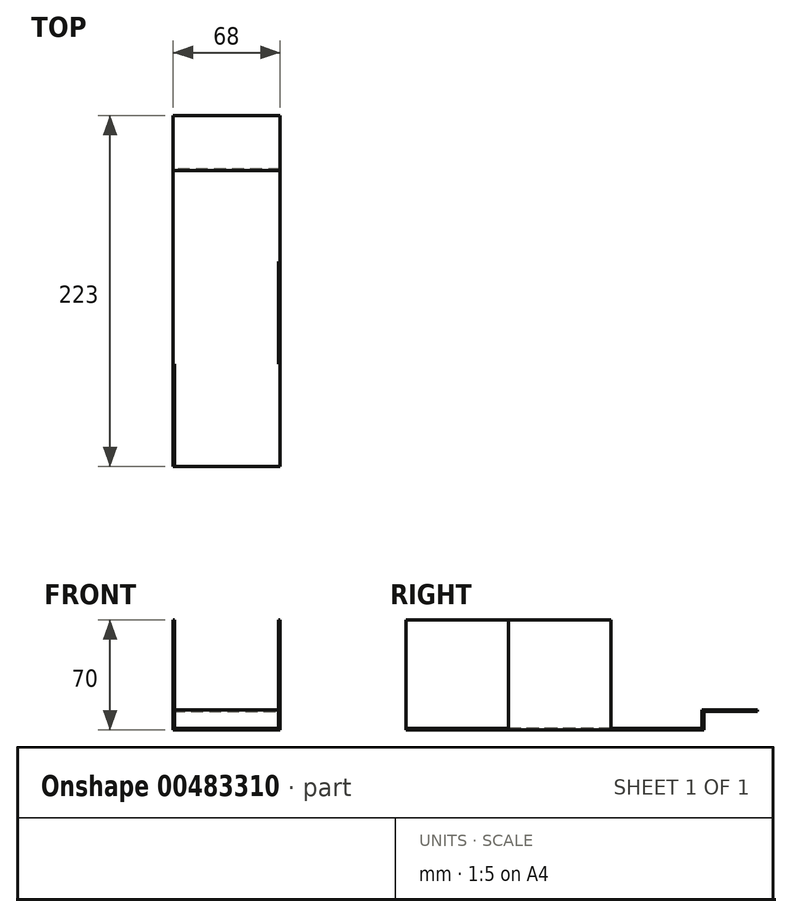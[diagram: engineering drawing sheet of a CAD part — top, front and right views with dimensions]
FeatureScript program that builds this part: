
annotation { "Feature Type Name" : "Feature", "Feature Type Description" : "" }
export const myFeature = defineFeature(function(context is Context, id is Id, definition is map)
    precondition{}
    {
        {
            var Q0;
            Q0=qCreatedBy(makeId("Top.planeOp"),FACE);
            var sketch = newSketch(context, id + "F0", { "sketchPlane" : qUnion([Q0])});
            skLineSegment(sketch, "E0.bottom", {"start": v(111.94, 131.54) * mm, "end": v(179.94, 131.54) * mm});
            skLineSegment(sketch, "E0.top", {"start": v(111.94, -91.46) * mm, "end": v(179.94, -91.46) * mm});
            skLineSegment(sketch, "E0.left", {"start": v(111.94, 131.54) * mm, "end": v(111.94, -91.46) * mm});
            skLineSegment(sketch, "E0.right", {"start": v(179.94, 131.54) * mm, "end": v(179.94, -91.46) * mm});
            skLineSegment(sketch, "E1.top", {"start": v(111.94, 96.54) * mm, "end": v(179.94, 96.54) * mm});
            skLineSegment(sketch, "E1.left", {"start": v(111.94, 131.54) * mm, "end": v(111.94, 96.54) * mm});
            skLineSegment(sketch, "E1.right", {"start": v(179.94, 131.54) * mm, "end": v(179.94, 96.54) * mm});
            skSolve(sketch);
        }
        {
            var Q0;
            Q0=makeQuery(id+"F0.imprint","IMPRINT",FACE,{"disambiguationData":[TD([[makeQuery(id+"F0.imprint","IMPRINT",EDGE,{"derivedFrom":sQuery(id+"F0.wireOp",EDGE,"E0.top")}),1.0]])]});
            extrude(context, id + "F1", {"entities" : qUnion([Q0]), "depth" : 1 * mm});
        }
        {
            var Q0;
            Q0=makeQuery(id+"F0.imprint","IMPRINT",FACE,{"disambiguationData":[TD([[makeQuery(id+"F0.imprint","IMPRINT",EDGE,{"derivedFrom":sQuery(id+"F0.wireOp",EDGE,"E0.bottom")}),-1.0]])]});
            extrude(context, id + "F2", {"entities" : qUnion([Q0]), "operationType" : NewBodyOperationType.ADD, "depth" : 13 * mm});
        }
        {
            var Q0;
            {var subQ0=sQuery(id+"F0.wireOp",EDGE,"E1.top");Q0=makeQuery(id+"F2.boolean.opBoolean","MERGE",FACE,{"derivedFrom":[makeQuery(id+"F1.opExtrude","CAP_FACE",FACE,{"disambiguationData":[OSD([sQuery(id+"F0.wireOp",EDGE,"E0.top"),sQuery(id+"F0.wireOp",EDGE,"E0.left"),sQuery(id+"F0.wireOp",EDGE,"E0.right"),subQ0])],"isStart":true}),makeQuery(id+"F2.opExtrude","CAP_FACE",FACE,{"disambiguationData":[OSD([sQuery(id+"F0.wireOp",EDGE,"E0.bottom"),subQ0,sQuery(id+"F0.wireOp",EDGE,"E1.left"),sQuery(id+"F0.wireOp",EDGE,"E1.right")])],"isStart":true})]});}
            var sketch = newSketch(context, id + "F3", { "sketchPlane" : qUnion([Q0])});
            skLineSegment(sketch, "E2.bottom", {"start": v(179.94, -131.54) * mm, "end": v(111.94, -131.54) * mm});
            skLineSegment(sketch, "E2.top", {"start": v(179.94, -97.54) * mm, "end": v(111.94, -97.54) * mm});
            skLineSegment(sketch, "E2.left", {"start": v(179.94, -131.54) * mm, "end": v(179.94, -97.54) * mm});
            skLineSegment(sketch, "E2.right", {"start": v(111.94, -131.54) * mm, "end": v(111.94, -97.54) * mm});
            skSolve(sketch);
        }
        {
            var Q0;
            Q0=makeQuery(id+"F3.imprint","IMPRINT",FACE,{"disambiguationData":[TD([[makeQuery(id+"F3.imprint","IMPRINT",EDGE,{"derivedFrom":sQuery(id+"F3.wireOp",EDGE,"E2.bottom")}),1.0]])]});
            extrude(context, id + "F4", {"entities" : qUnion([Q0]), "operationType" : NewBodyOperationType.REMOVE, "oppositeDirection" : true, "depth" : 12 * mm});
        }
        {
            var Q0;
            Q0=makeQuery(id+"F2.boolean.opBoolean","MERGE",FACE,{"derivedFrom":[makeQuery(id+"F1.opExtrude","SWEPT_FACE",FACE,{"disambiguationData":[OSD([sQuery(id+"F0.wireOp",EDGE,"E0.right")])]}),makeQuery(id+"F2.opExtrude","SWEPT_FACE",FACE,{"disambiguationData":[OSD([sQuery(id+"F0.wireOp",EDGE,"E1.right")])]})]});
            var sketch = newSketch(context, id + "F5", { "sketchPlane" : qUnion([Q0])});
            skLineSegment(sketch, "E3.right", {"start": v(-26.46, 0) * mm, "end": v(-26.46, 70) * mm});
            skLineSegment(sketch, "E4.bottom", {"start": v(-26.46, 0) * mm, "end": v(38.54, 0) * mm});
            skLineSegment(sketch, "E4.top", {"start": v(-26.46, 70) * mm, "end": v(38.54, 70) * mm});
            skLineSegment(sketch, "E4.right", {"start": v(38.54, 0) * mm, "end": v(38.54, 70) * mm});
            skSolve(sketch);
        }
        {
            var Q0;
            {var subQ0=sQuery(id+"F5.wireOp",EDGE,"E3.top");Q0=makeQuery(id+"F5.imprint","IMPRINT",FACE,{"disambiguationData":[TD([[makeQuery(id+"F5.imprint","IMPRINT",EDGE,{"derivedFrom":subQ0}),-1.0]])]});}
            var Q1;
            {var subQ0=sQuery(id+"F5.wireOp",EDGE,"E4.top");Q1=makeQuery(id+"F5.imprint","IMPRINT",FACE,{"disambiguationData":[TD([[makeQuery(id+"F5.imprint","IMPRINT",EDGE,{"derivedFrom":subQ0}),-1.0]])]});}
            extrude(context, id + "F6", {"entities" : qUnion([Q0, Q1]), "operationType" : NewBodyOperationType.ADD, "oppositeDirection" : true, "depth" : 1 * mm});
        }
        {
            var Q0;
            Q0=makeQuery(id+"F2.boolean.opBoolean","MERGE",FACE,{"derivedFrom":[makeQuery(id+"F1.opExtrude","SWEPT_FACE",FACE,{"disambiguationData":[OSD([sQuery(id+"F0.wireOp",EDGE,"E0.left")])]}),makeQuery(id+"F2.opExtrude","SWEPT_FACE",FACE,{"disambiguationData":[OSD([sQuery(id+"F0.wireOp",EDGE,"E1.left")])]})]});
            var sketch = newSketch(context, id + "F7", { "sketchPlane" : qUnion([Q0])});
            skLineSegment(sketch, "E5.bottom", {"start": v(91.46, 0) * mm, "end": v(26.46, 0) * mm});
            skLineSegment(sketch, "E5.top", {"start": v(91.46, 70) * mm, "end": v(26.46, 70) * mm});
            skLineSegment(sketch, "E5.left", {"start": v(91.46, 0) * mm, "end": v(91.46, 70) * mm});
            skLineSegment(sketch, "E5.right", {"start": v(26.46, 0) * mm, "end": v(26.46, 70) * mm});
            skSolve(sketch);
        }
        {
            var Q0;
            {var subQ0=sQuery(id+"F7.wireOp",EDGE,"E5.top");Q0=makeQuery(id+"F7.imprint","IMPRINT",FACE,{"disambiguationData":[TD([[makeQuery(id+"F7.imprint","IMPRINT",EDGE,{"derivedFrom":subQ0}),1.0]])]});}
            extrude(context, id + "F8", {"entities" : qUnion([Q0]), "operationType" : NewBodyOperationType.ADD, "oppositeDirection" : true, "depth" : 1 * mm});
        }
        {
            var Q0;
            Q0=makeQuery(id+"F1.opExtrude","SWEPT_BODY",BODY,{"disambiguationData":[OSD([sQuery(id+"F0.wireOp",EDGE,"E0.top"),sQuery(id+"F0.wireOp",EDGE,"E0.left"),sQuery(id+"F0.wireOp",EDGE,"E0.right"),sQuery(id+"F0.wireOp",EDGE,"E1.top")])]});
            transform(context, id + "F9", {"entities" : qUnion([Q0]), "transformType" : TransformType.TRANSLATION_3D, "dx" : -146.44 * mm, "dy" : 0 * mm, "dz" : 0 * mm, "makeCopy" : false});
        }
    });
